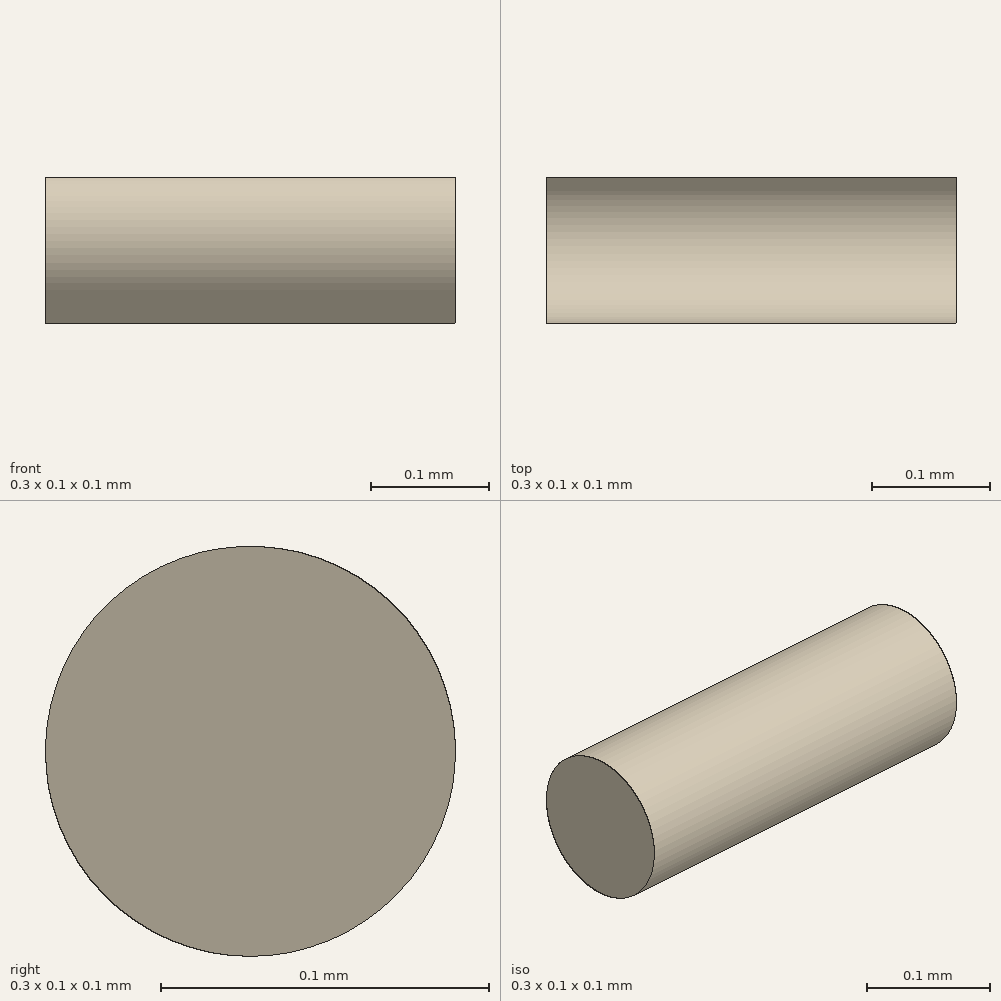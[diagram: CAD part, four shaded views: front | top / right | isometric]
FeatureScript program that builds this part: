
annotation { "Feature Type Name" : "Feature", "Feature Type Description" : "" }
export const myFeature = defineFeature(function(context is Context, id is Id, definition is map)
    precondition{}
    {
        {
            var Q0;
            Q0=qCreatedBy(makeId("Right.planeOp"),FACE);
            var sketch = newSketch(context, id + "F0", { "sketchPlane" : qUnion([Q0])});
            skCircle(sketch, "E0", {"center": v(0, 0) * mm, "radius": 0.06 * mm});
            skSolve(sketch);
        }
        {
            var Q0;
            Q0 = qSketchRegion(id + "F0", true);
            extrude(context, id + "F1", {"entities" : qUnion([Q0]), "depth" : 0.35 * mm, "offsetDistance" : 25 * mm});
        }
    });
